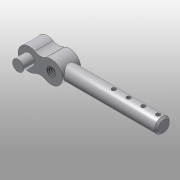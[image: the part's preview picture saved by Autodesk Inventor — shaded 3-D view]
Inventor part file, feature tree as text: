
AUTODESK INVENTOR PART (.ipt)
format: ipt  version: 2015 (Build 190159000, 159)  size: 122,368 bytes
history: native  units: mm
features: sketch x4, other x3
ambient origin geometry x8: Origin, YZ Plane, XZ Plane, XY Plane, X Axis, Y Axis, Z Axis, Center Point
bodies: Solid1 (feature_tree)
feature tree (7):
  other  "500-178.ipt"
  other  "Solid1::500-178.ipt"
  other  "TaggingFeature1"
  sketch  "Sketch1"  dims[d0=10.0mm]
  sketch  "Sketch2"
  sketch  "Sketch3"
  sketch  "Sketch4"
